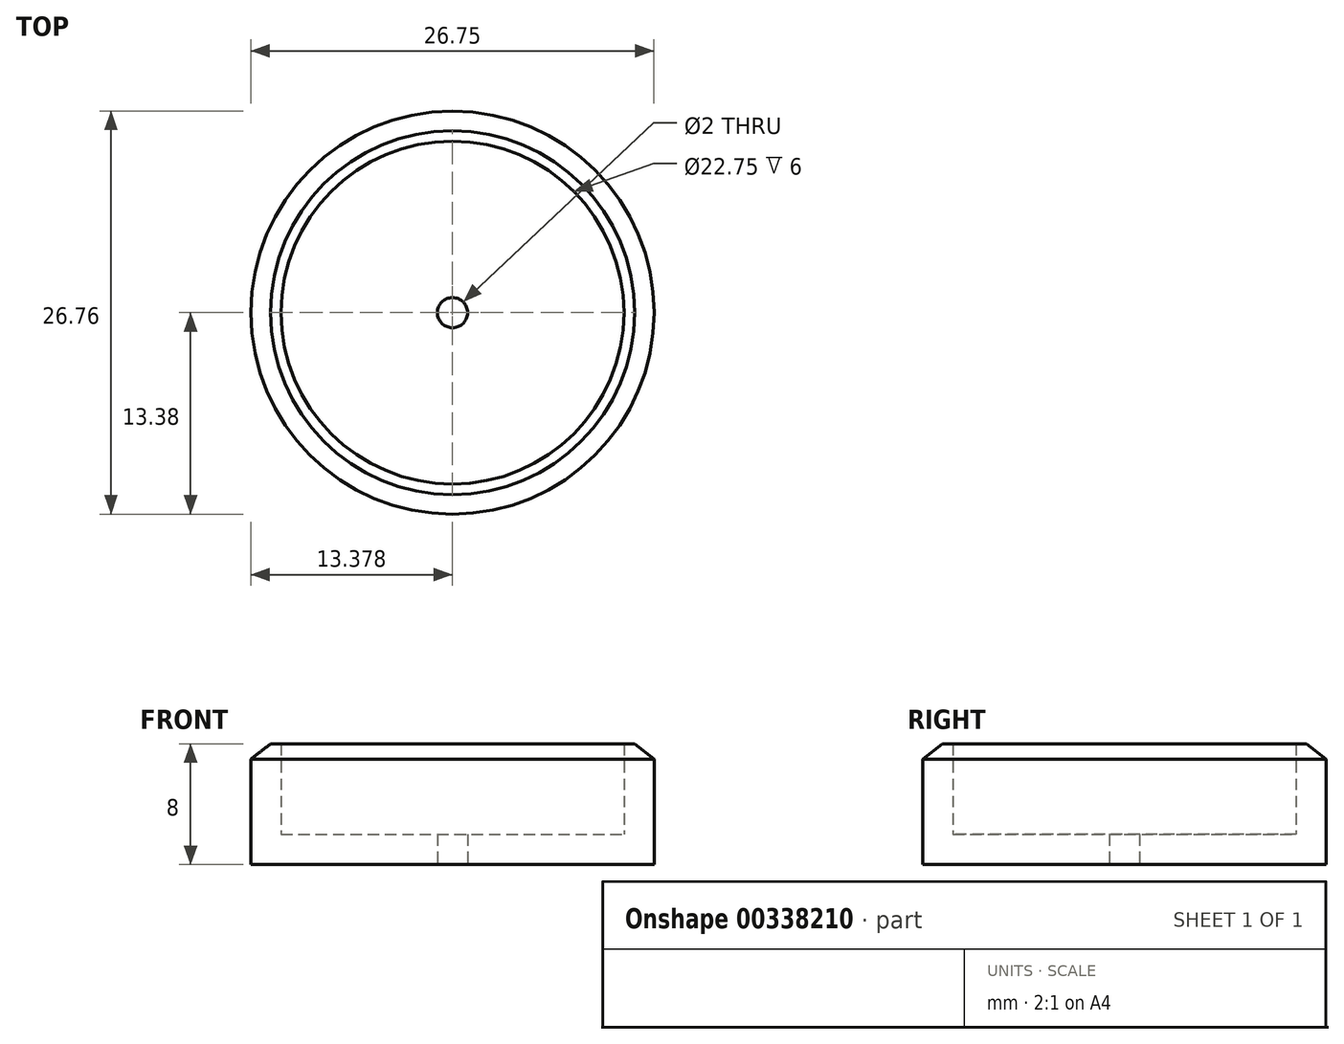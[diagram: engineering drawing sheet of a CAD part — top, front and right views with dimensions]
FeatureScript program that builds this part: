
annotation { "Feature Type Name" : "Feature", "Feature Type Description" : "" }
export const myFeature = defineFeature(function(context is Context, id is Id, definition is map)
    precondition{}
    {
        {
            var Q0;
            Q0=qCreatedBy(makeId("Front.planeOp"),FACE);
            var sketch = newSketch(context, id + "F0", { "sketchPlane" : qUnion([Q0])});
            skLineSegment(sketch, "E0", {"start": v(3.45, -5.78) * mm, "end": v(3.45, -3.78) * mm, "construction": true});
            skLineSegment(sketch, "E1", {"start": v(3.45, -5.78) * mm, "end": v(2.45, -5.78) * mm, "construction": true});
            skLineSegment(sketch, "E2", {"start": v(2.45, -5.78) * mm, "end": v(2.45, -3.78) * mm, "construction": true});
            skLineSegment(sketch, "E3", {"start": v(2.45, -3.78) * mm, "end": v(3.45, -3.78) * mm, "construction": true});
            skLineSegment(sketch, "E4", {"start": v(2.45, -5.78) * mm, "end": v(-9.93, -5.78) * mm});
            skLineSegment(sketch, "E5", {"start": v(2.45, -3.78) * mm, "end": v(-7.93, -3.78) * mm});
            skLineSegment(sketch, "E6", {"start": v(-9.93, 1.22) * mm, "end": v(-9.93, -5.78) * mm});
            skLineSegment(sketch, "E7", {"start": v(-9.93, 1.22) * mm, "end": v(-8.63, 2.22) * mm});
            skLineSegment(sketch, "E8", {"start": v(-8.63, 2.22) * mm, "end": v(-7.93, 2.22) * mm});
            skLineSegment(sketch, "E9", {"start": v(2.45, -3.78) * mm, "end": v(2.45, -5.78) * mm});
            skPoint(sketch, "E10.end.orphan", {"position": v(-7.93, 1.22) * mm});
            skLineSegment(sketch, "E11", {"start": v(-7.93, -3.78) * mm, "end": v(-7.93, 2.22) * mm});
            skSolve(sketch);
        }
        {
            var Q0;
            Q0 = qSketchRegion(id + "F0", true);
            var Q1;
            Q1=sQuery(id+"F0.wireOp",EDGE,"E0");
            revolve(context, id + "F1", {"entities" : qUnion([Q0]), "axis" : qUnion([Q1]), "revolveType" : RevolveType.FULL});
        }
    });
